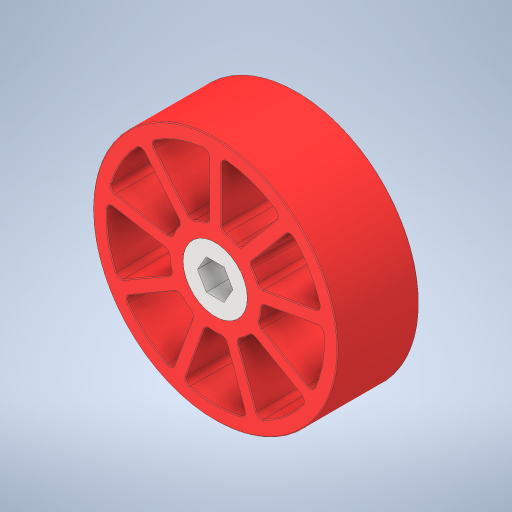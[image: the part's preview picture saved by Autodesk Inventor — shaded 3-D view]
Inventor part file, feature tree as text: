
AUTODESK INVENTOR PART (.ipt)
format: ipt  version: 2023.4 (Build 274418000, 418)  size: 1,051,136 bytes
history: native  units: in
note: dims shown in document units (in); Inventor stores cm internally (conversion verified against a paired STEP export)
features: other x2, plane x1
ambient origin geometry x8: Origin, YZ Plane, XZ Plane, XY Plane, X Axis, Y Axis, Z Axis, Center Point
bodies: Solid1 (feature_tree), Solid2 (feature_tree)
feature tree (3):
  plane  "Work Plane1"
  other  "3IN Molded Compliant Wheel Tread VER2-1-solid1"
  other  "am-3947-1000 375H x 1000IN Spacer-1-solid1"
